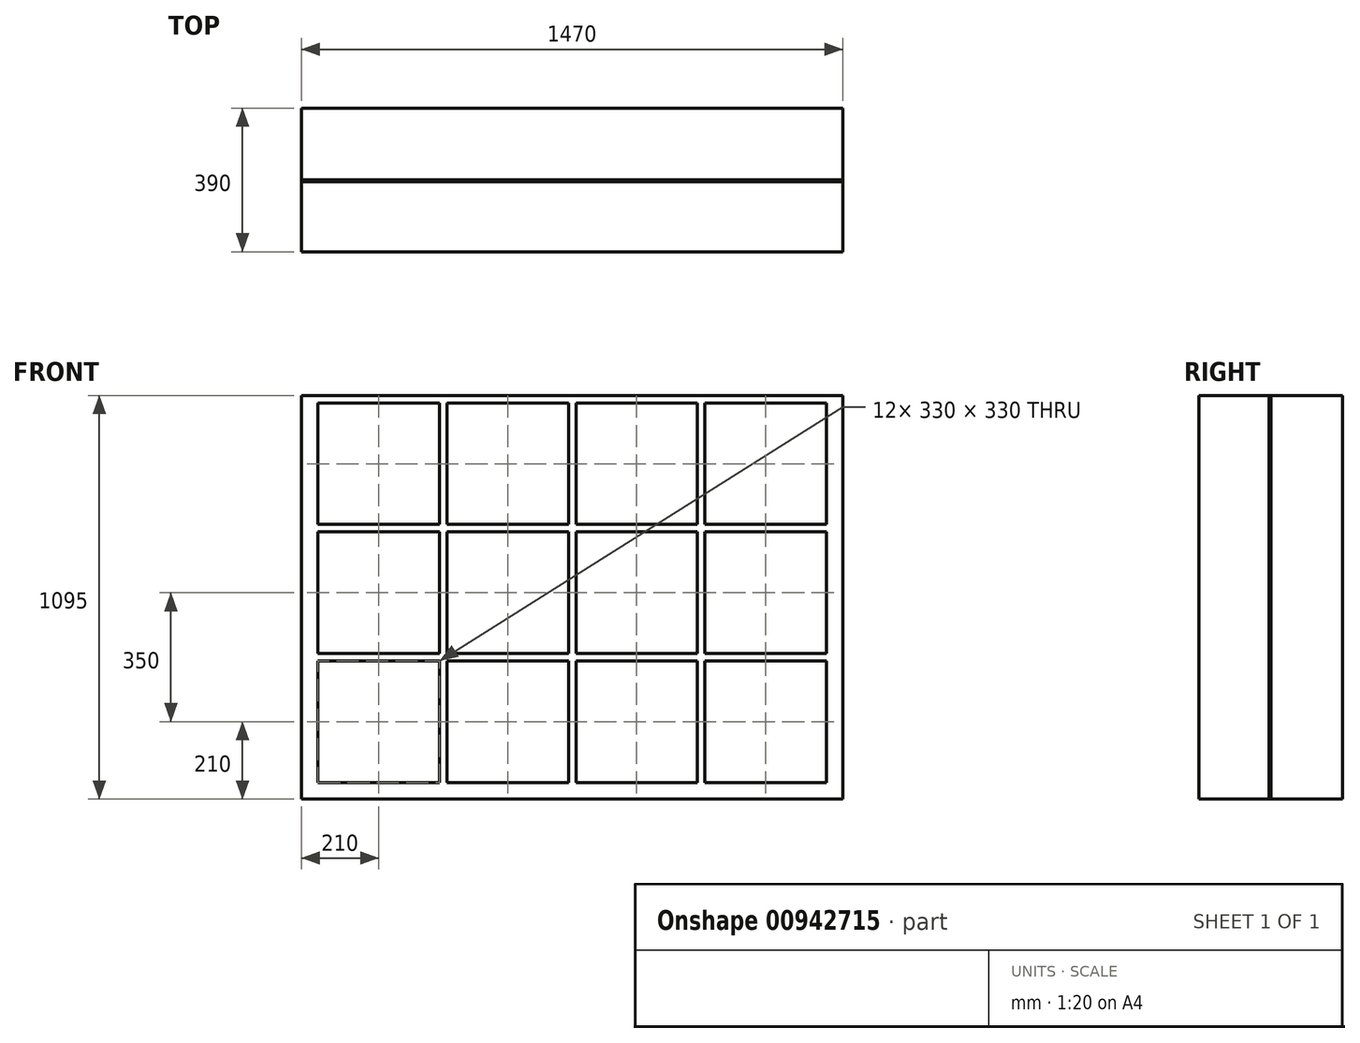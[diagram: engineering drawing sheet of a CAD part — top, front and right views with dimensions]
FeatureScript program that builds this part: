
annotation { "Feature Type Name" : "Feature", "Feature Type Description" : "" }
export const myFeature = defineFeature(function(context is Context, id is Id, definition is map)
    precondition{}
    {
        {
            var Q0;
            Q0=qCreatedBy(makeId("Front.planeOp"),FACE);
            var sketch = newSketch(context, id + "F0", { "sketchPlane" : qUnion([Q0])});
            skLineSegment(sketch, "E0.bottom", {"start": v(-735, 735) * mm, "end": v(735, 735) * mm});
            skLineSegment(sketch, "E0.top", {"start": v(-735, -735) * mm, "end": v(735, -735) * mm});
            skLineSegment(sketch, "E0.left", {"start": v(-735, 735) * mm, "end": v(-735, -735) * mm});
            skLineSegment(sketch, "E0.right", {"start": v(735, 735) * mm, "end": v(735, -735) * mm});
            skLineSegment(sketch, "E1", {"start": v(-735, 0) * mm, "end": v(0, 0) * mm, "construction": true});
            skLineSegment(sketch, "E2", {"start": v(0, 0) * mm, "end": v(735, 0) * mm, "construction": true});
            skLineSegment(sketch, "E3", {"start": v(0, -735) * mm, "end": v(0, 0) * mm, "construction": true});
            skLineSegment(sketch, "E4", {"start": v(0, 0) * mm, "end": v(0, 735) * mm, "construction": true});
            skLineSegment(sketch, "E5.bottom", {"start": v(-690, 690) * mm, "end": v(-360, 690) * mm});
            skLineSegment(sketch, "E5.top", {"start": v(-690, 360) * mm, "end": v(-360, 360) * mm});
            skLineSegment(sketch, "E5.left", {"start": v(-690, 690) * mm, "end": v(-690, 360) * mm});
            skLineSegment(sketch, "E5.right", {"start": v(-360, 690) * mm, "end": v(-360, 360) * mm});
            skLineSegment(sketch, "E6.bottom", {"start": v(-340, 360) * mm, "end": v(-10, 360) * mm});
            skLineSegment(sketch, "E6.top", {"start": v(-340, 690) * mm, "end": v(-10, 690) * mm});
            skLineSegment(sketch, "E6.left", {"start": v(-340, 360) * mm, "end": v(-340, 690) * mm});
            skLineSegment(sketch, "E6.right", {"start": v(-10, 360) * mm, "end": v(-10, 690) * mm});
            skLineSegment(sketch, "E7.bottom", {"start": v(10, 360) * mm, "end": v(340, 360) * mm});
            skLineSegment(sketch, "E7.top", {"start": v(10, 690) * mm, "end": v(340, 690) * mm});
            skLineSegment(sketch, "E7.left", {"start": v(10, 360) * mm, "end": v(10, 690) * mm});
            skLineSegment(sketch, "E7.right", {"start": v(340, 360) * mm, "end": v(340, 690) * mm});
            skLineSegment(sketch, "E8.bottom", {"start": v(360, 360) * mm, "end": v(690, 360) * mm});
            skLineSegment(sketch, "E8.top", {"start": v(360, 690) * mm, "end": v(690, 690) * mm});
            skLineSegment(sketch, "E8.left", {"start": v(360, 360) * mm, "end": v(360, 690) * mm});
            skLineSegment(sketch, "E8.right", {"start": v(690, 360) * mm, "end": v(690, 690) * mm});
            skLineSegment(sketch, "E9.bottom", {"start": v(-690, 10) * mm, "end": v(-360, 10) * mm});
            skLineSegment(sketch, "E9.top", {"start": v(-690, 340) * mm, "end": v(-360, 340) * mm});
            skLineSegment(sketch, "E9.left", {"start": v(-690, 10) * mm, "end": v(-690, 340) * mm});
            skLineSegment(sketch, "E9.right", {"start": v(-360, 10) * mm, "end": v(-360, 340) * mm});
            skLineSegment(sketch, "E10.bottom", {"start": v(-340, 10) * mm, "end": v(-10, 10) * mm});
            skLineSegment(sketch, "E10.top", {"start": v(-340, 340) * mm, "end": v(-10, 340) * mm});
            skLineSegment(sketch, "E10.left", {"start": v(-340, 10) * mm, "end": v(-340, 340) * mm});
            skLineSegment(sketch, "E10.right", {"start": v(-10, 10) * mm, "end": v(-10, 340) * mm});
            skLineSegment(sketch, "E11.bottom", {"start": v(10, 10) * mm, "end": v(340, 10) * mm});
            skLineSegment(sketch, "E11.top", {"start": v(10, 340) * mm, "end": v(340, 340) * mm});
            skLineSegment(sketch, "E11.left", {"start": v(10, 10) * mm, "end": v(10, 340) * mm});
            skLineSegment(sketch, "E11.right", {"start": v(340, 10) * mm, "end": v(340, 340) * mm});
            skLineSegment(sketch, "E12.bottom", {"start": v(360, 10) * mm, "end": v(690, 10) * mm});
            skLineSegment(sketch, "E12.top", {"start": v(360, 340) * mm, "end": v(690, 340) * mm});
            skLineSegment(sketch, "E12.left", {"start": v(360, 10) * mm, "end": v(360, 340) * mm});
            skLineSegment(sketch, "E12.right", {"start": v(690, 10) * mm, "end": v(690, 340) * mm});
            skLineSegment(sketch, "E13.MirrorCS", {"start": v(-690, -10) * mm, "end": v(-360, -10) * mm});
            skLineSegment(sketch, "E14.MirrorCS", {"start": v(-360, -10) * mm, "end": v(-360, -340) * mm});
            skLineSegment(sketch, "E15.MirrorCS", {"start": v(-690, -340) * mm, "end": v(-360, -340) * mm});
            skLineSegment(sketch, "E16.MirrorCS", {"start": v(-690, -10) * mm, "end": v(-690, -340) * mm});
            skLineSegment(sketch, "E17.MirrorCS", {"start": v(-690, -360) * mm, "end": v(-360, -360) * mm});
            skLineSegment(sketch, "E18.MirrorCS", {"start": v(-690, -690) * mm, "end": v(-690, -360) * mm});
            skLineSegment(sketch, "E19.MirrorCS", {"start": v(-690, -690) * mm, "end": v(-360, -690) * mm});
            skLineSegment(sketch, "E20.MirrorCS", {"start": v(-360, -690) * mm, "end": v(-360, -360) * mm});
            skLineSegment(sketch, "E21.MirrorCS", {"start": v(-340, -690) * mm, "end": v(-10, -690) * mm});
            skLineSegment(sketch, "E22.MirrorCS", {"start": v(-340, -360) * mm, "end": v(-340, -690) * mm});
            skLineSegment(sketch, "E23.MirrorCS", {"start": v(-340, -360) * mm, "end": v(-10, -360) * mm});
            skLineSegment(sketch, "E24.MirrorCS", {"start": v(-10, -360) * mm, "end": v(-10, -690) * mm});
            skLineSegment(sketch, "E25.MirrorCS", {"start": v(-340, -340) * mm, "end": v(-10, -340) * mm});
            skLineSegment(sketch, "E26.MirrorCS", {"start": v(-340, -10) * mm, "end": v(-340, -340) * mm});
            skLineSegment(sketch, "E27.MirrorCS", {"start": v(-340, -10) * mm, "end": v(-10, -10) * mm});
            skLineSegment(sketch, "E28.MirrorCS", {"start": v(-10, -10) * mm, "end": v(-10, -340) * mm});
            skLineSegment(sketch, "E29.MirrorCS", {"start": v(10, -340) * mm, "end": v(340, -340) * mm});
            skLineSegment(sketch, "E30.MirrorCS", {"start": v(10, -360) * mm, "end": v(340, -360) * mm});
            skLineSegment(sketch, "E31.MirrorCS", {"start": v(10, -360) * mm, "end": v(10, -690) * mm});
            skLineSegment(sketch, "E32.MirrorCS", {"start": v(10, -10) * mm, "end": v(10, -340) * mm});
            skLineSegment(sketch, "E33.MirrorCS", {"start": v(10, -10) * mm, "end": v(340, -10) * mm});
            skLineSegment(sketch, "E34.MirrorCS", {"start": v(340, -10) * mm, "end": v(340, -340) * mm});
            skLineSegment(sketch, "E35.MirrorCS", {"start": v(340, -360) * mm, "end": v(340, -690) * mm});
            skLineSegment(sketch, "E36.MirrorCS", {"start": v(10, -690) * mm, "end": v(340, -690) * mm});
            skLineSegment(sketch, "E37.MirrorCS", {"start": v(360, -690) * mm, "end": v(690, -690) * mm});
            skLineSegment(sketch, "E38.MirrorCS", {"start": v(690, -360) * mm, "end": v(690, -690) * mm});
            skLineSegment(sketch, "E39.MirrorCS", {"start": v(360, -360) * mm, "end": v(690, -360) * mm});
            skLineSegment(sketch, "E40.MirrorCS", {"start": v(360, -340) * mm, "end": v(690, -340) * mm});
            skLineSegment(sketch, "E41.MirrorCS", {"start": v(360, -360) * mm, "end": v(360, -690) * mm});
            skLineSegment(sketch, "E42.MirrorCS", {"start": v(360, -10) * mm, "end": v(360, -340) * mm});
            skLineSegment(sketch, "E43.MirrorCS", {"start": v(360, -10) * mm, "end": v(690, -10) * mm});
            skLineSegment(sketch, "E44.MirrorCS", {"start": v(690, -10) * mm, "end": v(690, -340) * mm});
            skSolve(sketch);
        }
        {
            var Q0;
            Q0=makeQuery(id+"F0.imprint","IMPRINT",FACE,{"disambiguationData":[TD([[makeQuery(id+"F0.imprint","IMPRINT",EDGE,{"derivedFrom":sQuery(id+"F0.wireOp",EDGE,"E0.bottom")}),-1.0]])]});
            extrude(context, id + "F1", {"entities" : qUnion([Q0]), "depth" : 390 * mm, "offsetDistance" : 25 * mm, "symmetric" : true});
        }
        {
            var Q0;
            Q0 = qSketchRegion(id + "F0", true);
            var Q1;
            Q1=makeQuery(id+"F0.imprint","IMPRINT",FACE,{"disambiguationData":[TD([[makeQuery(id+"F0.imprint","IMPRINT",EDGE,{"derivedFrom":sQuery(id+"F0.wireOp",EDGE,"E8.bottom")}),1.0]])]});
            var Q2;
            Q2=makeQuery(id+"F0.imprint","IMPRINT",FACE,{"disambiguationData":[TD([[makeQuery(id+"F0.imprint","IMPRINT",EDGE,{"derivedFrom":sQuery(id+"F0.wireOp",EDGE,"E7.bottom")}),1.0]])]});
            var Q3;
            Q3=makeQuery(id+"F0.imprint","IMPRINT",FACE,{"disambiguationData":[TD([[makeQuery(id+"F0.imprint","IMPRINT",EDGE,{"derivedFrom":sQuery(id+"F0.wireOp",EDGE,"E6.bottom")}),1.0]])]});
            var Q4;
            Q4=makeQuery(id+"F0.imprint","IMPRINT",FACE,{"disambiguationData":[TD([[makeQuery(id+"F0.imprint","IMPRINT",EDGE,{"derivedFrom":sQuery(id+"F0.wireOp",EDGE,"E5.bottom")}),-1.0]])]});
            var Q5;
            Q5=makeQuery(id+"F0.imprint","IMPRINT",FACE,{"disambiguationData":[TD([[makeQuery(id+"F0.imprint","IMPRINT",EDGE,{"derivedFrom":sQuery(id+"F0.wireOp",EDGE,"E9.bottom")}),1.0]])]});
            var Q6;
            Q6=makeQuery(id+"F0.imprint","IMPRINT",FACE,{"disambiguationData":[TD([[makeQuery(id+"F0.imprint","IMPRINT",EDGE,{"derivedFrom":sQuery(id+"F0.wireOp",EDGE,"E10.bottom")}),1.0]])]});
            var Q7;
            Q7=makeQuery(id+"F0.imprint","IMPRINT",FACE,{"disambiguationData":[TD([[makeQuery(id+"F0.imprint","IMPRINT",EDGE,{"derivedFrom":sQuery(id+"F0.wireOp",EDGE,"E25.MirrorCS")}),1.0]])]});
            var Q8;
            Q8=makeQuery(id+"F0.imprint","IMPRINT",FACE,{"disambiguationData":[TD([[makeQuery(id+"F0.imprint","IMPRINT",EDGE,{"derivedFrom":sQuery(id+"F0.wireOp",EDGE,"E13.MirrorCS")}),-1.0]])]});
            var Q9;
            Q9=makeQuery(id+"F0.imprint","IMPRINT",FACE,{"disambiguationData":[TD([[makeQuery(id+"F0.imprint","IMPRINT",EDGE,{"derivedFrom":sQuery(id+"F0.wireOp",EDGE,"E17.MirrorCS")}),-1.0]])]});
            var Q10;
            Q10=makeQuery(id+"F0.imprint","IMPRINT",FACE,{"disambiguationData":[TD([[makeQuery(id+"F0.imprint","IMPRINT",EDGE,{"derivedFrom":sQuery(id+"F0.wireOp",EDGE,"E21.MirrorCS")}),1.0]])]});
            var Q11;
            Q11=makeQuery(id+"F0.imprint","IMPRINT",FACE,{"disambiguationData":[TD([[makeQuery(id+"F0.imprint","IMPRINT",EDGE,{"derivedFrom":sQuery(id+"F0.wireOp",EDGE,"E30.MirrorCS")}),-1.0]])]});
            var Q12;
            Q12=makeQuery(id+"F0.imprint","IMPRINT",FACE,{"disambiguationData":[TD([[makeQuery(id+"F0.imprint","IMPRINT",EDGE,{"derivedFrom":sQuery(id+"F0.wireOp",EDGE,"E37.MirrorCS")}),1.0]])]});
            var Q13;
            Q13=makeQuery(id+"F0.imprint","IMPRINT",FACE,{"disambiguationData":[TD([[makeQuery(id+"F0.imprint","IMPRINT",EDGE,{"derivedFrom":sQuery(id+"F0.wireOp",EDGE,"E40.MirrorCS")}),1.0]])]});
            var Q14;
            Q14=makeQuery(id+"F0.imprint","IMPRINT",FACE,{"disambiguationData":[TD([[makeQuery(id+"F0.imprint","IMPRINT",EDGE,{"derivedFrom":sQuery(id+"F0.wireOp",EDGE,"E12.bottom")}),1.0]])]});
            var Q15;
            Q15=makeQuery(id+"F0.imprint","IMPRINT",FACE,{"disambiguationData":[TD([[makeQuery(id+"F0.imprint","IMPRINT",EDGE,{"derivedFrom":sQuery(id+"F0.wireOp",EDGE,"E11.bottom")}),1.0]])]});
            var Q16;
            Q16=makeQuery(id+"F0.imprint","IMPRINT",FACE,{"disambiguationData":[TD([[makeQuery(id+"F0.imprint","IMPRINT",EDGE,{"derivedFrom":sQuery(id+"F0.wireOp",EDGE,"E29.MirrorCS")}),1.0]])]});
            extrude(context, id + "F2", {"entities" : qUnion([Q0, Q1, Q2, Q3, Q4, Q5, Q6, Q7, Q8, Q9, Q10, Q11, Q12, Q13, Q14, Q15, Q16]), "depth" : 5 * mm, "offsetDistance" : 25 * mm});
        }
        {
            var Q0;
            Q0=makeQuery(id+"F1.opExtrude","SWEPT_FACE",FACE,{"disambiguationData":[OSD([sQuery(id+"F0.wireOp",EDGE,"E0.bottom")])]});
            var Q1;
            Q1=makeQuery(id+"F1.opExtrude","SWEPT_FACE",FACE,{"disambiguationData":[OSD([sQuery(id+"F0.wireOp",EDGE,"E6.bottom")])]});
            extrude(context, id + "F3", {"entities" : qUnion([Q0]), "operationType" : NewBodyOperationType.REMOVE, "endBound" : BoundingType.UP_TO_SURFACE, "oppositeDirection" : true, "depth" : 25 * mm, "endBoundEntityFace" : qUnion([Q1]), "offsetDistance" : 25 * mm});
        }
    });
